# Revit family: Slider with Trim-4Panel
name_source: partatom
category: Windows
revit_build: Autodesk Revit Architecture 2012 (Build: 20110309_2315(x64)
units: mm (PartAtom-declared; Revit-internal decimal feet)

## types (12) — shared parameters
Assembly Code = B2020100
Glass Pane Material = Glass
Sash Material = Sash
Trim Exterior Material = Trim
Trim Projection - Ext. = 0' - 0 3/4"
Trim Projection - Int. = 0' - 0 3/4"
Trim Width - Exterior = 0' - 3 1/2"
Trim Width - Interior = 0' - 3 1/2"
Wall Closure = By host
Window Inset = 0' - 0 3/4"

## per-type parameters (varying)
| type | Default Sill Height | Height | Keynote | Rough Height | Rough Width | Trim Interior Material | Width | mullion width | mullion-horiz-distance |
| 36" x 48" | 3' - 0" | 5' - 0" |  | 0' - 0" | 0' - 0" | Trim | 6' - 0" | 0' - 1" | 1' - 2 1/4" |
| 36" x 24" | 3' - 0" | 2' - 0" |  | 0' - 0" | 0' - 0" | Trim | 3' - 0" | 0' - 1" | 0' - 5 1/4" |
| 60" x 24" | 3' - 0" | 2' - 0" |  | 0' - 0" | 0' - 0" | Trim | 5' - 0" | 0' - 1" | 0' - 5 1/4" |
| 60" x 48" | 3' - 0" | 4' - 0" |  | 0' - 0" | 0' - 0" | Trim | 5' - 0" | 0' - 5 3/4" | 0' - 11 1/4" |
| 48" x 24" | 3' - 0" | 2' - 0" |  | 0' - 0" | 0' - 0" | Trim | 4' - 0" | 0' - 5 3/4" | 0' - 5 1/4" |
| 48" x 48" | 3' - 0" | 4' - 0" |  | 0' - 0" | 0' - 0" | Trim | 4' - 0" | 0' - 1" | 0' - 11 1/4" |
| Transom12" x 60" | 6' - 8" | 1' - 0" |  | 0' - 0" | 0' - 0" | Trim | 5' - 0" | 0' - 1" | 0' - 2 1/4" |
| 24" x 36" | 3' - 0" | 3' - 0" | SLIDER | 3' - 0" | 2' - 0" | Trim | 2' - 0" | 0' - 1" | 0' - 8 1/4" |
| 36" x 36" | 3' - 0" | 3' - 0" | SLIDER | 3' - 0" | 3' - 0" | Trim-Interior | 3' - 0" | 0' - 1" | 0' - 8 1/4" |
| 40" x 36" | 3' - 8" | 3' - 0" | SLIDER | 3' - 0" | 3' - 4" | Trim | 3' - 4" | 0' - 1" | 0' - 8 1/4" |
| 30" x 36" | 3' - 0" | 3' - 0" | SLIDER | 3' - 0" | 2' - 6" | Trim | 2' - 6" | 0' - 1" | 0' - 8 1/4" |
| 44" x 36" | 3' - 8" | 3' - 0" | SLIDER | 3' - 0" | 3' - 8" | Trim-Interior | 3' - 8" | 0' - 1" | 0' - 8 1/4" |

## geometry (parser evidence)
native form markers: Sweep x1
no freeform markers — native parametric forms only
